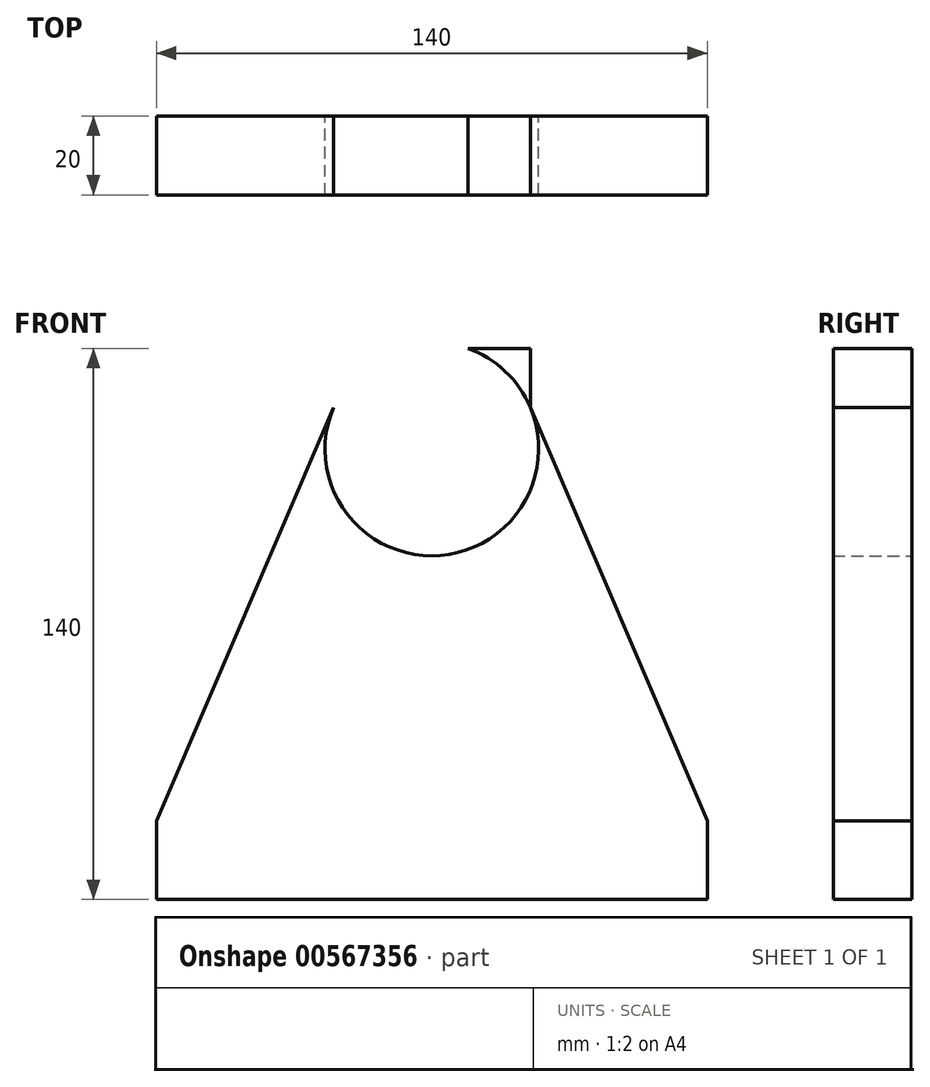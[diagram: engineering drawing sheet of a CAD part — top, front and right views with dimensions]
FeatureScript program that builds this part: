
annotation { "Feature Type Name" : "Feature", "Feature Type Description" : "" }
export const myFeature = defineFeature(function(context is Context, id is Id, definition is map)
    precondition{}
    {
        {
            var Q0;
            Q0=qCreatedBy(makeId("Front.planeOp"),FACE);
            var sketch = newSketch(context, id + "F0", { "sketchPlane" : qUnion([Q0])});
            skLineSegment(sketch, "E0.bottom", {"start": v(-140, 140) * mm, "end": v(0, 140) * mm});
            skLineSegment(sketch, "E0.top", {"start": v(-140, 0) * mm, "end": v(0, 0) * mm});
            skLineSegment(sketch, "E0.left", {"start": v(-140, 140) * mm, "end": v(-140, 0) * mm});
            skLineSegment(sketch, "E0.right", {"start": v(0, 140) * mm, "end": v(0, 0) * mm});
            skLineSegment(sketch, "E1.top", {"start": v(-140, 20) * mm, "end": v(0, 20) * mm});
            skLineSegment(sketch, "E1.left", {"start": v(-140, 0) * mm, "end": v(-140, 20) * mm});
            skLineSegment(sketch, "E1.right", {"start": v(0, 0) * mm, "end": v(0, 20) * mm});
            skLineSegment(sketch, "E2", {"start": v(-140, 140) * mm, "end": v(-95, 140) * mm});
            skLineSegment(sketch, "E3", {"start": v(0, 140) * mm, "end": v(-45, 140) * mm});
            skLineSegment(sketch, "E4", {"start": v(-95, 140) * mm, "end": v(-95, 125) * mm});
            skLineSegment(sketch, "E5", {"start": v(-45, 140) * mm, "end": v(-45, 125) * mm});
            skCircle(sketch, "E6", {"center": v(-70, 114.44) * mm, "radius": 27.14 * mm});
            skPoint(sketch, "E6.third.point", {"position": v(-52.86, 135.48) * mm});
            skLineSegment(sketch, "E7", {"start": v(-95, 125) * mm, "end": v(-140, 20) * mm});
            skLineSegment(sketch, "E8", {"start": v(-45, 125) * mm, "end": v(0, 20) * mm});
            skSolve(sketch);
        }
        {
            var Q0;
            {var subQ0=sQuery(id+"F0.wireOp",EDGE,"E6");var subQ1=sQuery(id+"F0.wireOp",EDGE,"E0.bottom");var subQ2=makeQuery(id+"F0.imprint","INTERSECT",VERTEX,{"disambiguationData":[OD(0.0)],"derivedFrom":[subQ1,subQ0]});Q0=makeQuery(id+"F0.imprint","IMPRINT",FACE,{"disambiguationData":[TD([[makeQuery(id+"F0.imprint","IMPRINT",EDGE,{"disambiguationData":[TD([[subQ2,-1.0]])],"derivedFrom":subQ1}),1.0]])]});}
            var Q1;
            Q1=makeQuery(id+"F0.imprint","IMPRINT",FACE,{"disambiguationData":[TD([[makeQuery(id+"F0.imprint","IMPRINT",EDGE,{"derivedFrom":sQuery(id+"F0.wireOp",EDGE,"E0.top")}),1.0]])]});
            var Q2;
            {var subQ0=sQuery(id+"F0.wireOp",EDGE,"E6");var subQ1=sQuery(id+"F0.wireOp",EDGE,"E0.bottom");var subQ2=makeQuery(id+"F0.imprint","INTERSECT",VERTEX,{"disambiguationData":[OD(0.0)],"derivedFrom":[subQ1,subQ0]});Q2=makeQuery(id+"F0.imprint","IMPRINT",FACE,{"disambiguationData":[TD([[makeQuery(id+"F0.imprint","IMPRINT",EDGE,{"disambiguationData":[TD([[subQ2,-1.0]])],"derivedFrom":subQ1}),-1.0]])]});}
            var Q3;
            Q3=makeQuery(id+"F0.imprint","IMPRINT",FACE,{"disambiguationData":[TD([[makeQuery(id+"F0.imprint","IMPRINT",EDGE,{"derivedFrom":sQuery(id+"F0.wireOp",EDGE,"E1.top")}),1.0]])]});
            extrude(context, id + "F1", {"entities" : qUnion([Q0, Q1, Q2, Q3]), "depth" : 20 * mm, "offsetDistance" : 25 * mm});
        }
        {
            var Q0;
            Q0=makeQuery(id+"F1.opExtrude","CAP_FACE",FACE,{"disambiguationData":[OSD([sQuery(id+"F0.wireOp",EDGE,"E0.top"),sQuery(id+"F0.wireOp",EDGE,"E1.left"),sQuery(id+"F0.wireOp",EDGE,"E1.right"),sQuery(id+"F0.wireOp",EDGE,"E6"),sQuery(id+"F0.wireOp",EDGE,"E7"),sQuery(id+"F0.wireOp",EDGE,"E8")])],"isStart":false});
            var sketch = newSketch(context, id + "F2", { "sketchPlane" : qUnion([Q0])});
            skLineSegment(sketch, "E9", {"start": v(-70, 141.58) * mm, "end": v(-70, 121.58) * mm});
            skPoint(sketch, "E9.endSnap0", {"position": v(-70, 141.58) * mm});
            skCircle(sketch, "E10", {"center": v(-70, 121.58) * mm, "radius": 11 * mm});
            skSolve(sketch);
        }
        {
            var Q0;
            Q0 = qSketchRegion(id + "F2", true);
            extrude(context, id + "F3", {"entities" : qUnion([Q0]), "operationType" : NewBodyOperationType.REMOVE, "oppositeDirection" : true, "depth" : 5 * mm, "offsetDistance" : 25 * mm});
        }
    });
